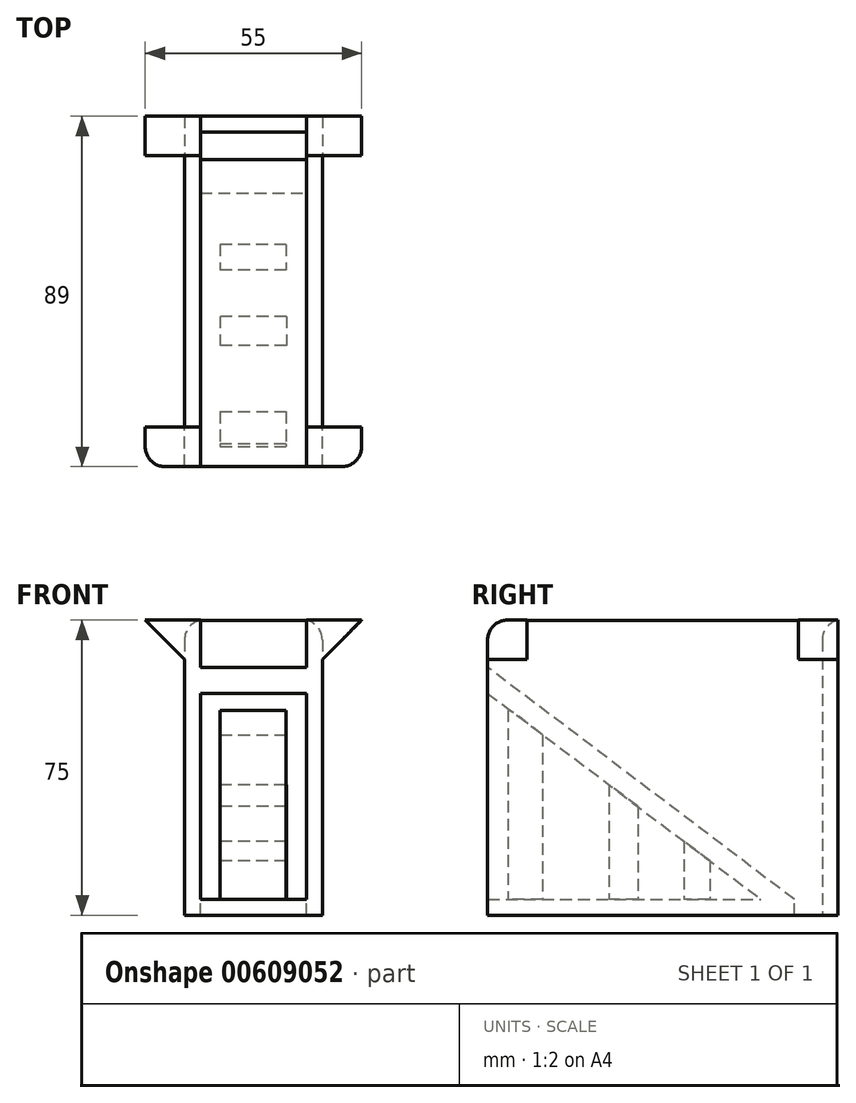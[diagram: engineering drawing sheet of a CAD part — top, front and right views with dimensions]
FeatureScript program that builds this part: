
annotation { "Feature Type Name" : "Feature", "Feature Type Description" : "" }
export const myFeature = defineFeature(function(context is Context, id is Id, definition is map)
    precondition{}
    {
        {
            var Q0;
            Q0=qCreatedBy(makeId("Top.planeOp"),FACE);
            var sketch = newSketch(context, id + "F0", { "sketchPlane" : qUnion([Q0])});
            skLineSegment(sketch, "E0.bottom", {"start": v(17.5, -44.5) * mm, "end": v(-17.5, -44.5) * mm});
            skLineSegment(sketch, "E0.top", {"start": v(17.5, 44.5) * mm, "end": v(-17.5, 44.5) * mm});
            skLineSegment(sketch, "E0.left", {"start": v(17.5, -44.5) * mm, "end": v(17.5, 44.5) * mm});
            skLineSegment(sketch, "E0.right", {"start": v(-17.5, -44.5) * mm, "end": v(-17.5, 44.5) * mm});
            skPoint(sketch, "E0.middle", {"position": v(0, 0) * mm});
            skSolve(sketch);
        }
        {
            var Q0;
            Q0=makeQuery(id+"F0.imprint","IMPRINT",FACE,{"disambiguationData":[TD([[makeQuery(id+"F0.imprint","IMPRINT",EDGE,{"derivedFrom":sQuery(id+"F0.wireOp",EDGE,"E0.bottom")}),-1.0]])]});
            extrude(context, id + "F1", {"entities" : qUnion([Q0]), "depth" : 63 * mm, "offsetDistance" : 25 * mm});
        }
        {
            var Q0;
            Q0=makeQuery(id+"F1.opExtrude","CAP_FACE",FACE,{"disambiguationData":[OSD([sQuery(id+"F0.wireOp",EDGE,"E0.bottom"),sQuery(id+"F0.wireOp",EDGE,"E0.top"),sQuery(id+"F0.wireOp",EDGE,"E0.left"),sQuery(id+"F0.wireOp",EDGE,"E0.right")])],"isStart":false});
            shell(context, id + "F2", {"entities" : qUnion([Q0]), "thickness" : 4 * mm});
        }
        {
            var Q0;
            Q0=makeQuery(id+"F2.opShell","OFFSET_FACE",FACE,{"disambiguationData":[OSD([sQuery(id+"F0.wireOp",EDGE,"E0.bottom"),sQuery(id+"F0.wireOp",EDGE,"E0.top"),sQuery(id+"F0.wireOp",EDGE,"E0.left"),sQuery(id+"F0.wireOp",EDGE,"E0.right")])]});
            var sketch = newSketch(context, id + "F3", { "sketchPlane" : qUnion([Q0])});
            skLineSegment(sketch, "E1.bottom", {"start": v(-13.5, 40.5) * mm, "end": v(13.5, 40.5) * mm});
            skLineSegment(sketch, "E1.top", {"start": v(-13.5, 33.45) * mm, "end": v(13.5, 33.45) * mm});
            skLineSegment(sketch, "E1.left", {"start": v(-13.5, 40.5) * mm, "end": v(-13.5, 33.45) * mm});
            skLineSegment(sketch, "E1.right", {"start": v(13.5, 40.5) * mm, "end": v(13.5, 33.45) * mm});
            skSolve(sketch);
        }
        {
            var Q0;
            Q0=makeQuery(id+"F3.imprint","IMPRINT",FACE,{"disambiguationData":[TD([[makeQuery(id+"F3.imprint","IMPRINT",EDGE,{"derivedFrom":sQuery(id+"F3.wireOp",EDGE,"E1.bottom")}),1.0]])]});
            extrude(context, id + "F4", {"entities" : qUnion([Q0]), "operationType" : NewBodyOperationType.REMOVE, "oppositeDirection" : true, "depth" : 4.3 * mm, "offsetDistance" : 25 * mm});
        }
        {
            var Q0;
            Q0=makeQuery(id+"F2.opShell","OFFSET_FACE",FACE,{"disambiguationData":[OSD([sQuery(id+"F0.wireOp",EDGE,"E0.bottom")])]});
            extrude(context, id + "F5", {"entities" : qUnion([Q0]), "operationType" : NewBodyOperationType.REMOVE, "oppositeDirection" : true, "depth" : 5.2 * mm, "offsetDistance" : 25 * mm});
        }
        {
            var Q0;
            {var subQ0=sQuery(id+"F0.wireOp",EDGE,"E0.left");Q0=makeQuery(id+"F5.boolean.opBoolean","MERGE",FACE,{"derivedFrom":[makeQuery(id+"F4.boolean.opBoolean","MERGE",FACE,{"derivedFrom":[makeQuery(id+"F2.opShell","OFFSET_FACE",FACE,{"disambiguationData":[OSD([subQ0])]}),makeQuery(id+"F4.opExtrude","SWEPT_FACE",FACE,{"disambiguationData":[OSD([sQuery(id+"F3.wireOp",EDGE,"E1.right")])]})]}),makeQuery(id+"F5.opExtrude","SWEPT_FACE",FACE,{"disambiguationData":[OSD([sQuery(id+"F0.wireOp",EDGE,"E0.bottom"),subQ0])]})]});}
            var sketch = newSketch(context, id + "F6", { "sketchPlane" : qUnion([Q0])});
            skLineSegment(sketch, "E2", {"start": v(-33.45, 4) * mm, "end": v(44.5, 63) * mm});
            skLineSegment(sketch, "E3", {"start": v(44.5, 63) * mm, "end": v(44.5, 56.42) * mm});
            skLineSegment(sketch, "E4", {"start": v(44.5, 56.42) * mm, "end": v(-24.96, 4) * mm});
            skLineSegment(sketch, "E5", {"start": v(-24.96, 4) * mm, "end": v(-33.45, 4) * mm});
            skSolve(sketch);
        }
        {
            var Q0;
            Q0=makeQuery(id+"F1.opExtrude","CAP_FACE",FACE,{"disambiguationData":[OSD([sQuery(id+"F0.wireOp",EDGE,"E0.bottom"),sQuery(id+"F0.wireOp",EDGE,"E0.top"),sQuery(id+"F0.wireOp",EDGE,"E0.left"),sQuery(id+"F0.wireOp",EDGE,"E0.right")])],"isStart":false});
            extrude(context, id + "F7", {"entities" : qUnion([Q0]), "operationType" : NewBodyOperationType.ADD, "depth" : 12 * mm, "offsetDistance" : 25 * mm});
        }
        {
            var Q0;
            {var subQ0=sQuery(id+"F3.wireOp",EDGE,"E1.top");Q0=makeQuery(id+"F3.imprint","IMPRINT",FACE,{"disambiguationData":[TD([[makeQuery(id+"F3.imprint","IMPRINT",EDGE,{"derivedFrom":subQ0}),-1.0]])]});}
            var sketch = newSketch(context, id + "F8", { "sketchPlane" : qUnion([Q0])});
            skLineSegment(sketch, "E6.bottom", {"start": v(8.32, 11.94) * mm, "end": v(-8.48, 11.94) * mm});
            skLineSegment(sketch, "E6.top", {"start": v(8.32, 5.4) * mm, "end": v(-8.48, 5.4) * mm});
            skLineSegment(sketch, "E6.left", {"start": v(8.32, 11.94) * mm, "end": v(8.32, 5.4) * mm});
            skLineSegment(sketch, "E6.right", {"start": v(-8.48, 11.94) * mm, "end": v(-8.48, 5.4) * mm});
            skLineSegment(sketch, "E7.bottom", {"start": v(8.39, -6.35) * mm, "end": v(-8.48, -6.35) * mm});
            skLineSegment(sketch, "E7.top", {"start": v(8.39, -13.7) * mm, "end": v(-8.48, -13.7) * mm});
            skLineSegment(sketch, "E7.left", {"start": v(8.39, -6.35) * mm, "end": v(8.39, -13.7) * mm});
            skLineSegment(sketch, "E7.right", {"start": v(-8.48, -6.35) * mm, "end": v(-8.48, -13.7) * mm});
            skLineSegment(sketch, "E8.bottom", {"start": v(-8.48, -30.53) * mm, "end": v(8.3, -30.53) * mm});
            skLineSegment(sketch, "E8.top", {"start": v(-8.48, -39.35) * mm, "end": v(8.3, -39.35) * mm});
            skLineSegment(sketch, "E8.left", {"start": v(-8.48, -30.53) * mm, "end": v(-8.48, -39.35) * mm});
            skLineSegment(sketch, "E8.right", {"start": v(8.3, -30.53) * mm, "end": v(8.3, -39.35) * mm});
            skSolve(sketch);
        }
        {
            var Q0;
            Q0=makeQuery(id+"F6.imprint","IMPRINT",FACE,{"disambiguationData":[TD([[makeQuery(id+"F6.imprint","IMPRINT",EDGE,{"derivedFrom":sQuery(id+"F6.wireOp",EDGE,"E2")}),-1.0]])]});
            extrude(context, id + "F9", {"entities" : qUnion([Q0]), "operationType" : NewBodyOperationType.ADD, "depth" : 28.5 * mm, "offsetDistance" : 25 * mm});
        }
        {
            var Q0;
            Q0=makeQuery(id+"F8.imprint","IMPRINT",FACE,{"disambiguationData":[TD([[makeQuery(id+"F8.imprint","IMPRINT",EDGE,{"derivedFrom":sQuery(id+"F8.wireOp",EDGE,"E6.bottom")}),1.0]])]});
            extrude(context, id + "F10", {"entities" : qUnion([Q0]), "operationType" : NewBodyOperationType.ADD, "depth" : 15.6 * mm, "offsetDistance" : 25 * mm});
        }
        {
            var Q0;
            Q0=makeQuery(id+"F8.imprint","IMPRINT",FACE,{"disambiguationData":[TD([[makeQuery(id+"F8.imprint","IMPRINT",EDGE,{"derivedFrom":sQuery(id+"F8.wireOp",EDGE,"E7.bottom")}),1.0]])]});
            extrude(context, id + "F11", {"entities" : qUnion([Q0]), "operationType" : NewBodyOperationType.ADD, "depth" : 29.2 * mm, "offsetDistance" : 25 * mm});
        }
        {
            var Q0;
            Q0=makeQuery(id+"F8.imprint","IMPRINT",FACE,{"disambiguationData":[TD([[makeQuery(id+"F8.imprint","IMPRINT",EDGE,{"derivedFrom":sQuery(id+"F8.wireOp",EDGE,"E8.bottom")}),-1.0]])]});
            extrude(context, id + "F12", {"entities" : qUnion([Q0]), "operationType" : NewBodyOperationType.ADD, "depth" : 48.1 * mm, "offsetDistance" : 25 * mm});
        }
        {
            var Q0;
            {var subQ0=sQuery(id+"F0.wireOp",EDGE,"E0.left");Q0=makeQuery(id+"F7.boolean.opBoolean","MERGE",FACE,{"derivedFrom":[makeQuery(id+"F1.opExtrude","SWEPT_FACE",FACE,{"disambiguationData":[OSD([subQ0])]}),makeQuery(id+"F7.opExtrude","SWEPT_FACE",FACE,{"disambiguationData":[OSD([subQ0])]})]});}
            var sketch = newSketch(context, id + "F13", { "sketchPlane" : qUnion([Q0])});
            skLineSegment(sketch, "E9.bottom", {"start": v(-44.5, 75) * mm, "end": v(-34.5, 75) * mm});
            skLineSegment(sketch, "E9.top", {"start": v(-44.5, 65) * mm, "end": v(-34.5, 65) * mm});
            skLineSegment(sketch, "E9.left", {"start": v(-44.5, 75) * mm, "end": v(-44.5, 65) * mm});
            skLineSegment(sketch, "E9.right", {"start": v(-34.5, 75) * mm, "end": v(-34.5, 65) * mm});
            skLineSegment(sketch, "E10.MirrorCS", {"start": v(44.5, 75) * mm, "end": v(44.5, 65) * mm});
            skLineSegment(sketch, "E11.MirrorCS", {"start": v(44.5, 75) * mm, "end": v(34.5, 75) * mm});
            skLineSegment(sketch, "E12.MirrorCS", {"start": v(34.5, 75) * mm, "end": v(34.5, 65) * mm});
            skLineSegment(sketch, "E13.MirrorCS", {"start": v(44.5, 65) * mm, "end": v(34.5, 65) * mm});
            skSolve(sketch);
        }
        {
            var Q0;
            Q0=makeQuery(id+"F13.imprint","IMPRINT",FACE,{"disambiguationData":[TD([[makeQuery(id+"F13.imprint","IMPRINT",EDGE,{"derivedFrom":sQuery(id+"F13.wireOp",EDGE,"E9.bottom")}),-1.0]])]});
            var Q1;
            Q1=makeQuery(id+"F13.imprint","IMPRINT",FACE,{"disambiguationData":[TD([[makeQuery(id+"F13.imprint","IMPRINT",EDGE,{"derivedFrom":sQuery(id+"F13.wireOp",EDGE,"E10.MirrorCS")}),-1.0]])]});
            extrude(context, id + "F14", {"entities" : qUnion([Q0, Q1]), "operationType" : NewBodyOperationType.ADD, "depth" : 10 * mm, "offsetDistance" : 25 * mm});
        }
        {
            var Q0;
            {var subQ0=sQuery(id+"F0.wireOp",EDGE,"E0.right");Q0=makeQuery(id+"F7.boolean.opBoolean","MERGE",FACE,{"derivedFrom":[makeQuery(id+"F1.opExtrude","SWEPT_FACE",FACE,{"disambiguationData":[OSD([subQ0])]}),makeQuery(id+"F7.opExtrude","SWEPT_FACE",FACE,{"disambiguationData":[OSD([subQ0])]})]});}
            var sketch = newSketch(context, id + "F15", { "sketchPlane" : qUnion([Q0])});
            skLineSegment(sketch, "E14.bottom", {"start": v(-44.5, 75) * mm, "end": v(-34.5, 75) * mm});
            skLineSegment(sketch, "E14.top", {"start": v(-44.5, 65) * mm, "end": v(-34.5, 65) * mm});
            skLineSegment(sketch, "E14.left", {"start": v(-44.5, 75) * mm, "end": v(-44.5, 65) * mm});
            skLineSegment(sketch, "E14.right", {"start": v(-34.5, 75) * mm, "end": v(-34.5, 65) * mm});
            skLineSegment(sketch, "E15.MirrorCS", {"start": v(44.5, 75) * mm, "end": v(34.5, 75) * mm});
            skLineSegment(sketch, "E16.MirrorCS", {"start": v(44.5, 65) * mm, "end": v(34.5, 65) * mm});
            skLineSegment(sketch, "E17.MirrorCS", {"start": v(44.5, 75) * mm, "end": v(44.5, 65) * mm});
            skLineSegment(sketch, "E18.MirrorCS", {"start": v(34.5, 75) * mm, "end": v(34.5, 65) * mm});
            skSolve(sketch);
        }
        {
            var Q0;
            Q0=makeQuery(id+"F15.imprint","IMPRINT",FACE,{"disambiguationData":[TD([[makeQuery(id+"F15.imprint","IMPRINT",EDGE,{"derivedFrom":sQuery(id+"F15.wireOp",EDGE,"E14.bottom")}),1.0]])]});
            var Q1;
            Q1=makeQuery(id+"F15.imprint","IMPRINT",FACE,{"disambiguationData":[TD([[makeQuery(id+"F15.imprint","IMPRINT",EDGE,{"derivedFrom":sQuery(id+"F15.wireOp",EDGE,"E15.MirrorCS")}),1.0]])]});
            extrude(context, id + "F16", {"entities" : qUnion([Q0, Q1]), "operationType" : NewBodyOperationType.ADD, "depth" : 10 * mm, "offsetDistance" : 25 * mm});
        }
        {
            var Q0;
            {var subQ0=sQuery(id+"F0.wireOp",EDGE,"E0.top");Q0=makeQuery(id+"F16.boolean.opBoolean","MERGE",FACE,{"derivedFrom":[makeQuery(id+"F14.boolean.opBoolean","MERGE",FACE,{"derivedFrom":[makeQuery(id+"F7.boolean.opBoolean","MERGE",FACE,{"derivedFrom":[makeQuery(id+"F1.opExtrude","SWEPT_FACE",FACE,{"disambiguationData":[OSD([subQ0])]}),makeQuery(id+"F7.opExtrude","SWEPT_FACE",FACE,{"disambiguationData":[OSD([subQ0]),TDD([makeQuery(id+"F1.opExtrude","CAP_EDGE",EDGE,{"disambiguationData":[OSD([subQ0])],"isStart":false})])]})]}),makeQuery(id+"F14.opExtrude","SWEPT_FACE",FACE,{"disambiguationData":[OSD([sQuery(id+"F13.wireOp",EDGE,"E10.MirrorCS")])]})]}),makeQuery(id+"F16.opExtrude","SWEPT_FACE",FACE,{"disambiguationData":[OSD([sQuery(id+"F15.wireOp",EDGE,"E14.left")])]})]});}
            var sketch = newSketch(context, id + "F17", { "sketchPlane" : qUnion([Q0])});
            skLineSegment(sketch, "E19", {"start": v(-27.5, 75) * mm, "end": v(-27.5, 65) * mm});
            skLineSegment(sketch, "E20", {"start": v(-27.5, 65) * mm, "end": v(-17.5, 65) * mm});
            skLineSegment(sketch, "E21", {"start": v(-17.5, 65) * mm, "end": v(-27.5, 75) * mm});
            skLineSegment(sketch, "E22", {"start": v(17.5, 65) * mm, "end": v(27.5, 75) * mm});
            skLineSegment(sketch, "E23", {"start": v(27.5, 75) * mm, "end": v(27.5, 65) * mm});
            skLineSegment(sketch, "E24", {"start": v(27.5, 65) * mm, "end": v(17.5, 65) * mm});
            skSolve(sketch);
        }
        {
            var Q0;
            {var subQ0=sQuery(id+"F0.wireOp",EDGE,"E0.right");var subQ1=sQuery(id+"F0.wireOp",EDGE,"E0.left");var subQ2=sQuery(id+"F0.wireOp",EDGE,"E0.bottom");var subQ4=makeQuery(id+"F1.opExtrude","SWEPT_FACE",FACE,{"disambiguationData":[OSD([subQ2])]});var subQ5=makeQuery(id+"F1.opExtrude","CAP_EDGE",EDGE,{"disambiguationData":[OSD([subQ2])],"isStart":false});Q0=makeQuery(id+"F16.boolean.opBoolean","MERGE",FACE,{"derivedFrom":[makeQuery(id+"F14.boolean.opBoolean","MERGE",FACE,{"derivedFrom":[makeQuery(id+"F9.boolean.opBoolean","MERGE",FACE,{"derivedFrom":[makeQuery(id+"F7.boolean.opBoolean","MERGE",FACE,{"derivedFrom":[subQ4,makeQuery(id+"F7.opExtrude","SWEPT_FACE",FACE,{"disambiguationData":[OSD([subQ2]),TDD([makeQuery(id+"F5.boolean.opBoolean","SPLIT",EDGE,{"disambiguationData":[TD([makeQuery(id+"F1.opExtrude","SWEPT_FACE",FACE,{"disambiguationData":[OSD([subQ1])]})])],"derivedFrom":subQ5})])]}),makeQuery(id+"F7.opExtrude","SWEPT_FACE",FACE,{"disambiguationData":[OSD([subQ2]),TDD([makeQuery(id+"F5.boolean.opBoolean","SPLIT",EDGE,{"disambiguationData":[TD([makeQuery(id+"F1.opExtrude","SWEPT_FACE",FACE,{"disambiguationData":[OSD([subQ0])]})])],"derivedFrom":subQ5})])]})]}),makeQuery(id+"F9.opExtrude","SWEPT_FACE",FACE,{"disambiguationData":[OSD([sQuery(id+"F6.wireOp",EDGE,"E3")])]})]}),makeQuery(id+"F14.opExtrude","SWEPT_FACE",FACE,{"disambiguationData":[OSD([sQuery(id+"F13.wireOp",EDGE,"E9.left")])]})]}),makeQuery(id+"F16.opExtrude","SWEPT_FACE",FACE,{"disambiguationData":[OSD([sQuery(id+"F15.wireOp",EDGE,"E17.MirrorCS")])]})]});}
            var sketch = newSketch(context, id + "F18", { "sketchPlane" : qUnion([Q0])});
            skLineSegment(sketch, "E25", {"start": v(-27.5, 75) * mm, "end": v(-17.5, 65) * mm});
            skLineSegment(sketch, "E26", {"start": v(-17.5, 65) * mm, "end": v(-27.5, 65) * mm});
            skLineSegment(sketch, "E27", {"start": v(-27.5, 65) * mm, "end": v(-27.5, 75) * mm});
            skLineSegment(sketch, "E28", {"start": v(17.5, 65) * mm, "end": v(27.5, 75) * mm});
            skLineSegment(sketch, "E29", {"start": v(27.5, 75) * mm, "end": v(27.5, 65) * mm});
            skLineSegment(sketch, "E30", {"start": v(27.5, 65) * mm, "end": v(17.5, 65) * mm});
            skSolve(sketch);
        }
        {
            var Q0;
            Q0=makeQuery(id+"F18.imprint","IMPRINT",FACE,{"disambiguationData":[TD([[makeQuery(id+"F18.imprint","IMPRINT",EDGE,{"derivedFrom":sQuery(id+"F18.wireOp",EDGE,"E25")}),-1.0]])]});
            var Q1;
            Q1=makeQuery(id+"F18.imprint","IMPRINT",FACE,{"disambiguationData":[TD([[makeQuery(id+"F18.imprint","IMPRINT",EDGE,{"derivedFrom":sQuery(id+"F18.wireOp",EDGE,"E28")}),-1.0]])]});
            extrude(context, id + "F19", {"entities" : qUnion([Q0, Q1]), "operationType" : NewBodyOperationType.REMOVE, "oppositeDirection" : true, "depth" : 10 * mm, "offsetDistance" : 25 * mm});
        }
        {
            var Q0;
            Q0=makeQuery(id+"F17.imprint","IMPRINT",FACE,{"disambiguationData":[TD([[makeQuery(id+"F17.imprint","IMPRINT",EDGE,{"derivedFrom":sQuery(id+"F17.wireOp",EDGE,"E19")}),1.0]])]});
            var Q1;
            Q1=makeQuery(id+"F17.imprint","IMPRINT",FACE,{"disambiguationData":[TD([[makeQuery(id+"F17.imprint","IMPRINT",EDGE,{"derivedFrom":sQuery(id+"F17.wireOp",EDGE,"E22")}),-1.0]])]});
            extrude(context, id + "F20", {"entities" : qUnion([Q0, Q1]), "operationType" : NewBodyOperationType.REMOVE, "oppositeDirection" : true, "depth" : 10 * mm, "offsetDistance" : 25 * mm});
        }
        {
            var Q0;
            Q0=makeQuery(id+"F7.opExtrude","CAP_EDGE",EDGE,{"disambiguationData":[OSD([sQuery(id+"F0.wireOp",EDGE,"E0.bottom"),sQuery(id+"F0.wireOp",EDGE,"E0.right")])],"isStart":false});
            var Q1;
            Q1=makeQuery(id+"F7.opExtrude","CAP_EDGE",EDGE,{"disambiguationData":[OSD([sQuery(id+"F0.wireOp",EDGE,"E0.bottom"),sQuery(id+"F0.wireOp",EDGE,"E0.left")])],"isStart":false});
            var Q2;
            {var subQ0=sQuery(id+"F0.wireOp",EDGE,"E0.top");Q2=makeQuery(id+"F7.opExtrude","CAP_EDGE",EDGE,{"disambiguationData":[OSD([subQ0]),TDD([makeQuery(id+"F2.opShell","OFFSET_EDGE",EDGE,{"disambiguationData":[OSD([subQ0]),TDD([makeQuery(id+"F1.opExtrude","CAP_EDGE",EDGE,{"disambiguationData":[OSD([subQ0])],"isStart":false})])]})])],"isStart":false});}
            fillet(context, id + "F21", {"entities" : qUnion([Q0, Q1, Q2]), "radius" : 5 * mm, "tangentPropagation" : true, "allowEdgeOverflow" : false});
        }
    });
